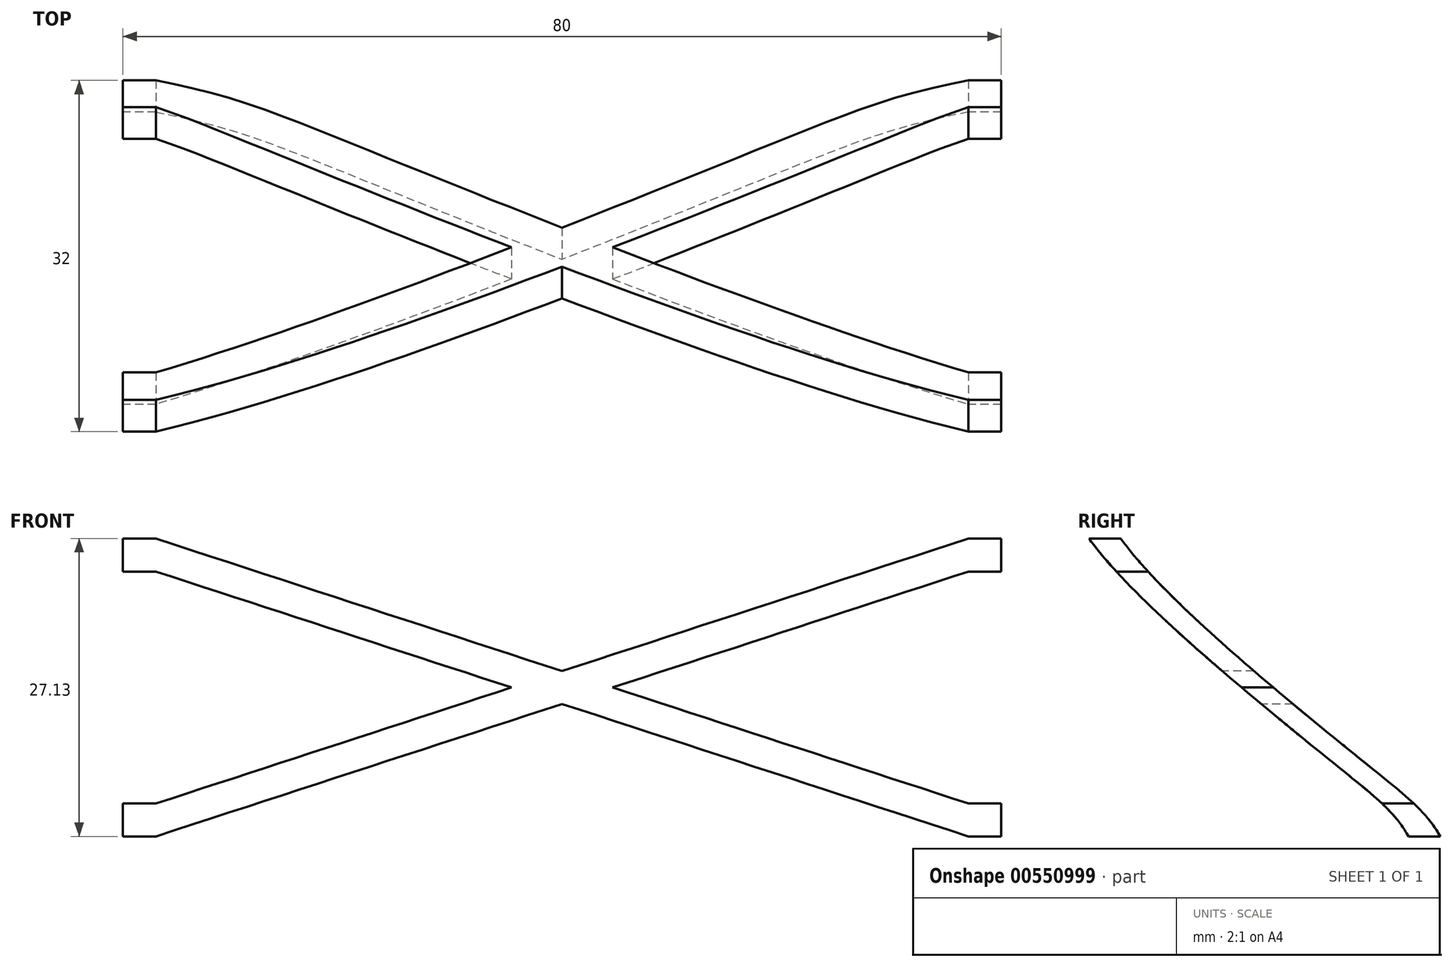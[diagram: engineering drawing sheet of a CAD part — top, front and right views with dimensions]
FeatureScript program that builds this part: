
annotation { "Feature Type Name" : "Feature", "Feature Type Description" : "" }
export const myFeature = defineFeature(function(context is Context, id is Id, definition is map)
    precondition{}
    {
        {
            var Q0;
            Q0=qCreatedBy(makeId("Right.planeOp"),FACE);
            var sketch = newSketch(context, id + "F0", { "sketchPlane" : qUnion([Q0])});
            skPoint(sketch, "E0", {"position": v(-182.2, 61.22) * mm});
            skPoint(sketch, "E1", {"position": v(-24.75, 54.2) * mm});
            skPoint(sketch, "E2", {"position": v(-35.08, 42.21) * mm});
            skPoint(sketch, "E3", {"position": v(21.95, -4.07) * mm});
            skPoint(sketch, "E4", {"position": v(21.95, -44.16) * mm});
            skPoint(sketch, "E5", {"position": v(40.96, -52.42) * mm});
            skPoint(sketch, "E6", {"position": v(40.96, -73.09) * mm});
            skLineSegment(sketch, "E7", {"start": v(-26.03, 52.72) * mm, "end": v(-35.08, 42.21) * mm});
            skPoint(sketch, "E8", {"position": v(-29.1, 49.16) * mm});
            skFitSpline(sketch, "E9", {"points": [v(-182.2, 61.22) * mm, v(-66.15, 57.24) * mm, v(-24.75, 54.2) * mm], "startDerivative": vector(208.84, -5.82) * mm, "endDerivative": vector(96.65, -8.45) * mm});
            skFitSpline(sketch, "E10", {"points": [v(21.95, -44.16) * mm, v(38.2, -50.23) * mm, v(40.96, -52.42) * mm, v(40.96, -73.09) * mm], "startDerivative": vector(49.63, -18.32) * mm, "endDerivative": vector(-4.17, -61.24) * mm});
            skLineSegment(sketch, "E11", {"start": v(21.95, -11.61) * mm, "end": v(21.95, -42.76) * mm});
            skFitSpline(sketch, "E12", {"points": [v(-43.05, 55.73) * mm, v(-42.8, 49.26) * mm, v(-35.08, 42.21) * mm, v(-12.08, 16.09) * mm, v(-1.02, -0.62) * mm, v(21.95, -4.07) * mm], "startDerivative": vector(-6.66, -55.67) * mm, "endDerivative": vector(115.26, 0.34) * mm});
            skFitSpline(sketch, "E13", {"points": [v(-35.08, 42.21) * mm, v(-13.95, 14.65) * mm, v(-1.02, -0.62) * mm], "startDerivative": vector(39.23, -52.2) * mm, "endDerivative": vector(28.4, -32.57) * mm});
            skFitSpline(sketch, "E14", {"points": [v(-13.95, 14.65) * mm, v(-4.8, 3.17) * mm], "startDerivative": vector(9.14, -11.49) * mm, "endDerivative": vector(9.14, -11.49) * mm});
            skFitSpline(sketch, "E15", {"points": [v(16.57, 3.53) * mm, v(20.72, -3.55) * mm, v(21.95, -11.61) * mm], "startDerivative": vector(9.75, -13.63) * mm, "endDerivative": vector(1, -16.65) * mm});
            skArc(sketch, "E16.filletArc", {"start": v(21.95, -42.76) * mm, "mid": v(22.3, -43.9) * mm, "end": v(23.25, -44.64) * mm});
            skFitSpline(sketch, "E17", {"points": [v(-29.92, 48.2) * mm, v(-4.34, 27.17) * mm, v(16.57, 3.53) * mm], "startDerivative": vector(52.63, -39.98) * mm, "endDerivative": vector(40.3, -49.4) * mm});
            skArc(sketch, "E18.filletArc", {"start": v(-26.03, 52.72) * mm, "mid": v(-25.86, 53.75) * mm, "end": v(-26.7, 54.37) * mm});
            skFitSpline(sketch, "E19", {"points": [v(21.95, -15.76) * mm, v(4.92, -15.96) * mm, v(-1.9, -18.86) * mm, v(-5.82, -30.22) * mm, v(-6.65, -34.35) * mm, v(-5.2, -36.42) * mm, v(21.95, -37.66) * mm], "startDerivative": vector(-87.15, 1.4) * mm, "endDerivative": vector(130.13, 2.89) * mm});
            skFitSpline(sketch, "E20", {"points": [v(9.26, -15.72) * mm, v(1.2, -19.06) * mm, v(-5.82, -30.22) * mm], "startDerivative": vector(-19.14, -4.54) * mm, "endDerivative": vector(-11.3, -23.76) * mm});
            skLineSegment(sketch, "E21.top", {"start": v(-19.35, 39.68) * mm, "end": v(-18.85, 39.68) * mm});
            skPoint(sketch, "E22.visualSharp", {"position": v(13.65, 63.27) * mm});
            skArc(sketch, "E22.filletArc", {"start": v(13.65, 61.27) * mm, "mid": v(13.07, 62.68) * mm, "end": v(11.65, 63.27) * mm});
            skPoint(sketch, "E23.visualSharp", {"position": v(-21.35, 39.68) * mm});
            skArc(sketch, "E23.filletArc", {"start": v(-21.35, 41.68) * mm, "mid": v(-20.76, 40.26) * mm, "end": v(-19.35, 39.68) * mm});
            skPoint(sketch, "E21.bottom.start.orphan", {"position": v(-21.35, 63.27) * mm});
            skFitSpline(sketch, "E24", {"points": [v(-10.57, 39.74) * mm, v(5.4, 25.26) * mm, v(20.88, 7.07) * mm, v(27.02, -4.97) * mm], "startDerivative": vector(44.88, -38.7) * mm, "endDerivative": vector(17.7, -41.42) * mm});
            skFitSpline(sketch, "E25", {"points": [v(25.38, -1.12) * mm, v(27.02, -4.97) * mm, v(23.37, -14.74) * mm, v(23.11, -17.09) * mm, v(23.25, -70.17) * mm], "startDerivative": vector(18.22, -20.9) * mm, "endDerivative": vector(-0.26, -138.73) * mm});
            skFitSpline(sketch, "E26", {"points": [v(4.07, 39.91) * mm, v(4.65, 34.35) * mm, v(28.76, 11.85) * mm, v(34.46, 6.15) * mm, v(36.65, -1.45) * mm, v(34.02, -12.4) * mm, v(37.24, -47.77) * mm, v(38.2, -71) * mm], "startDerivative": vector(-14.65, -54.98) * mm, "endDerivative": vector(-0.75, -120.7) * mm});
            skLineSegment(sketch, "E27.bottom", {"start": v(23.25, -70.17) * mm, "end": v(38.17, -70.17) * mm});
            skLineSegment(sketch, "E27.top", {"start": v(23.25, -61.5) * mm, "end": v(23.27, -61.5) * mm});
            skLineSegment(sketch, "E27.left", {"start": v(23.25, -70.17) * mm, "end": v(23.25, -61.5) * mm});
            skLineSegment(sketch, "E27.right", {"start": v(38.17, -70.17) * mm, "end": v(38.17, -61.5) * mm});
            skArc(sketch, "E28.filletArc", {"start": v(26.63, -6.95) * mm, "mid": v(26.82, -5.24) * mm, "end": v(26.42, -3.57) * mm});
            skFitSpline(sketch, "E29", {"points": [v(1.3, 37.92) * mm, v(1.3, 35.65) * mm, v(4.1, 31.83) * mm, v(10.5, 25.32) * mm, v(27.24, 10.65) * mm, v(29.93, 8.48) * mm, v(32.72, 4.86) * mm, v(33.96, 1.04) * mm], "startDerivative": vector(-4.6, -25.33) * mm, "endDerivative": vector(7.32, -33.09) * mm});
            skLineSegment(sketch, "E30", {"start": v(33.96, 1.04) * mm, "end": v(27.34, 1.04) * mm});
            skPoint(sketch, "E31.1.internal.orphan", {"position": v(26.1, 3.53) * mm});
            skFitSpline(sketch, "E32", {"points": [v(23.52, 6.83) * mm, v(25.06, 4.32) * mm, v(26.29, 1.76) * mm, v(26.49, 1.04) * mm], "startDerivative": vector(3.84, -5.9) * mm, "endDerivative": vector(0.63, -3) * mm});
            skLineSegment(sketch, "E33", {"start": v(27.34, 1.04) * mm, "end": v(26.49, 1.04) * mm});
            skCircle(sketch, "E34", {"center": v(28.45, -17.2) * mm, "radius": 3.64 * mm});
            skCircle(sketch, "E35", {"center": v(29.1, -28.19) * mm, "radius": 3.94 * mm});
            skCircle(sketch, "E36", {"center": v(29.75, -39.27) * mm, "radius": 4.69 * mm});
            skFitSpline(sketch, "E37", {"points": [v(-5.31, 35.2) * mm, v(-8.6, 39.74) * mm, v(-9.64, 46.84) * mm], "startDerivative": vector(-8.2, 8.8) * mm, "endDerivative": vector(-0.61, 14.37) * mm});
            skFitSpline(sketch, "E38", {"points": [v(3.65, 38.36) * mm, v(4.07, 43.99) * mm, v(4.9, 46.71) * mm], "startDerivative": vector(0.33, 10.52) * mm, "endDerivative": vector(2.28, 5.92) * mm});
            skLineSegment(sketch, "E39", {"start": v(4.9, 46.71) * mm, "end": v(-9.64, 46.84) * mm});
            skLineSegment(sketch, "E40", {"start": v(3.65, 38.36) * mm, "end": v(3.67, 37.52) * mm});
            skLineSegment(sketch, "E41", {"start": v(-3.63, 33.7) * mm, "end": v(-5.31, 35.2) * mm});
            skFitSpline(sketch, "E42", {"points": [v(-2.39, 35.11) * mm, v(-6.08, 38.28) * mm, v(-7.32, 43.27) * mm, v(-7.39, 44.92) * mm], "startDerivative": vector(-11.08, 6.69) * mm, "endDerivative": vector(-0.06, 6.14) * mm});
            skFitSpline(sketch, "E43", {"points": [v(1.3, 35.65) * mm, v(1.3, 39.08) * mm, v(1.94, 44.51) * mm], "startDerivative": vector(-0.25, 7.33) * mm, "endDerivative": vector(1.46, 10.28) * mm});
            skLineSegment(sketch, "E44", {"start": v(-7.39, 44.92) * mm, "end": v(2.05, 44.84) * mm});
            skLineSegment(sketch, "E45", {"start": v(2.05, 44.84) * mm, "end": v(1.94, 44.51) * mm});
            skLineSegment(sketch, "E46", {"start": v(-3.9, 36.07) * mm, "end": v(0, 32.89) * mm});
            skFitSpline(sketch, "E47.trimOffspring", {"points": [v(-5.4, 37.92) * mm, v(14.74, 18.2) * mm, v(23.52, 6.83) * mm], "startDerivative": vector(38.44, -35.72) * mm, "endDerivative": vector(18.29, -25.93) * mm});
            skArc(sketch, "E48.filletArc", {"start": v(1.3, 36) * mm, "mid": v(1.35, 35.59) * mm, "end": v(1.5, 35.2) * mm});
            skCircle(sketch, "E49", {"center": v(30.45, -51.2) * mm, "radius": 4.69 * mm});
            skCircle(sketch, "E50", {"center": v(31.14, -62.9) * mm, "radius": 4.69 * mm});
            skFitSpline(sketch, "E51", {"points": [v(6.96, 39.91) * mm, v(7.55, 34.35) * mm, v(31.65, 11.85) * mm, v(37.35, 6.15) * mm, v(39.54, -1.45) * mm, v(36.91, -12.4) * mm, v(40.13, -47.77) * mm, v(41.1, -71) * mm], "startDerivative": vector(-14.65, -54.98) * mm, "endDerivative": vector(-0.75, -120.7) * mm});
            skLineSegment(sketch, "E52", {"start": v(12.94, 34.54) * mm, "end": v(1.3, 35.65) * mm});
            skLineSegment(sketch, "E53", {"start": v(43.49, 5.85) * mm, "end": v(34.39, 2.69) * mm});
            skSolve(sketch);
        }
        {
            var Q0;
            {var subQ0=sQuery(id+"F0.wireOp",EDGE,"E52");var subQ1=sQuery(id+"F0.wireOp",EDGE,"E26");var subQ2=makeQuery(id+"F0.imprint","INTERSECT",VERTEX,{"derivedFrom":[subQ1,subQ0]});Q0=makeQuery(id+"F0.imprint","IMPRINT",FACE,{"disambiguationData":[TD([[makeQuery(id+"F0.imprint","IMPRINT",EDGE,{"disambiguationData":[TD([[subQ2,-1.0]])],"derivedFrom":subQ1}),1.0]])]});}
            extrude(context, id + "F1", {"entities" : qUnion([Q0]), "depth" : 80 * mm, "offsetDistance" : 25 * mm});
        }
        {
            var Q0;
            Q0=qCreatedBy(makeId("Front.planeOp"),FACE);
            var sketch = newSketch(context, id + "F2", { "sketchPlane" : qUnion([Q0])});
            skLineSegment(sketch, "E54.bottom", {"start": v(0, 33.15) * mm, "end": v(3, 33.15) * mm});
            skLineSegment(sketch, "E54.top", {"start": v(0, 6.02) * mm, "end": v(3, 6.02) * mm});
            skLineSegment(sketch, "E54.left", {"start": v(0, 33.15) * mm, "end": v(0, 30.15) * mm});
            skLineSegment(sketch, "E54.right", {"start": v(80, 33.15) * mm, "end": v(80, 30.15) * mm});
            skLineSegment(sketch, "E55", {"start": v(80, 30.15) * mm, "end": v(77, 30.15) * mm});
            skLineSegment(sketch, "E56", {"start": v(77, 30.15) * mm, "end": v(44.6, 19.58) * mm});
            skLineSegment(sketch, "E57", {"start": v(3, 9.02) * mm, "end": v(0, 9.02) * mm});
            skLineSegment(sketch, "E58", {"start": v(3, 9.02) * mm, "end": v(35.4, 19.58) * mm});
            skLineSegment(sketch, "E59.MirrorCS", {"start": v(0, 30.15) * mm, "end": v(3, 30.15) * mm});
            skLineSegment(sketch, "E60.MirrorCS", {"start": v(77, 9.02) * mm, "end": v(44.6, 19.58) * mm});
            skLineSegment(sketch, "E61.MirrorCS", {"start": v(3, 30.15) * mm, "end": v(35.4, 19.58) * mm});
            skLineSegment(sketch, "E62.MirrorCS", {"start": v(80, 33.15) * mm, "end": v(77, 33.15) * mm});
            skLineSegment(sketch, "E63.MirrorCS", {"start": v(77, 9.02) * mm, "end": v(80, 9.02) * mm});
            skLineSegment(sketch, "E64.MirrorCS", {"start": v(80, 6.02) * mm, "end": v(77, 6.02) * mm});
            skLineSegment(sketch, "E65.trimOffspring", {"start": v(40, 21.08) * mm, "end": v(77, 33.15) * mm});
            skLineSegment(sketch, "E66.trimOffspring", {"start": v(40, 18.08) * mm, "end": v(3, 6.02) * mm});
            skLineSegment(sketch, "E67.trimOffspring", {"start": v(40, 21.08) * mm, "end": v(3, 33.15) * mm});
            skLineSegment(sketch, "E68.trimOffspring", {"start": v(40, 18.08) * mm, "end": v(77, 6.02) * mm});
            skLineSegment(sketch, "E69.trimOffspring", {"start": v(3, 6.02) * mm, "end": v(0, 6.02) * mm});
            skLineSegment(sketch, "E70.trimOffspring", {"start": v(77, 33.15) * mm, "end": v(80, 33.15) * mm});
            skLineSegment(sketch, "E71.trimOffspring", {"start": v(3, 33.15) * mm, "end": v(0, 33.15) * mm});
            skLineSegment(sketch, "E72.trimOffspring", {"start": v(80, 9.02) * mm, "end": v(80, 6.02) * mm});
            skLineSegment(sketch, "E73", {"start": v(0, 9.02) * mm, "end": v(0, 6.02) * mm});
            skLineSegment(sketch, "E74.trimOffspring", {"start": v(77, 6.02) * mm, "end": v(80, 6.02) * mm});
            skPoint(sketch, "E75.trimOffspring.end.orphan", {"position": v(77, 6.02) * mm});
            skPoint(sketch, "E76.start.orphan", {"position": v(3, 33.15) * mm});
            skLineSegment(sketch, "E77.bottom", {"start": v(98.63, 47.34) * mm, "end": v(-16.63, 47.34) * mm});
            skLineSegment(sketch, "E77.top", {"start": v(98.63, -15.7) * mm, "end": v(-16.63, -15.7) * mm});
            skLineSegment(sketch, "E77.left", {"start": v(98.63, 47.34) * mm, "end": v(98.63, -15.7) * mm});
            skLineSegment(sketch, "E77.right", {"start": v(-16.63, 47.34) * mm, "end": v(-16.63, -15.7) * mm});
            skSolve(sketch);
        }
        {
            var Q0;
            Q0=makeQuery(id+"F2.imprint","IMPRINT",FACE,{"disambiguationData":[TD([[makeQuery(id+"F2.imprint","IMPRINT",EDGE,{"derivedFrom":sQuery(id+"F2.wireOp",EDGE,"E55")}),1.0]])]});
            extrude(context, id + "F3", {"entities" : qUnion([Q0]), "operationType" : NewBodyOperationType.REMOVE, "oppositeDirection" : true, "depth" : 50 * mm, "offsetDistance" : 25 * mm});
        }
    });
